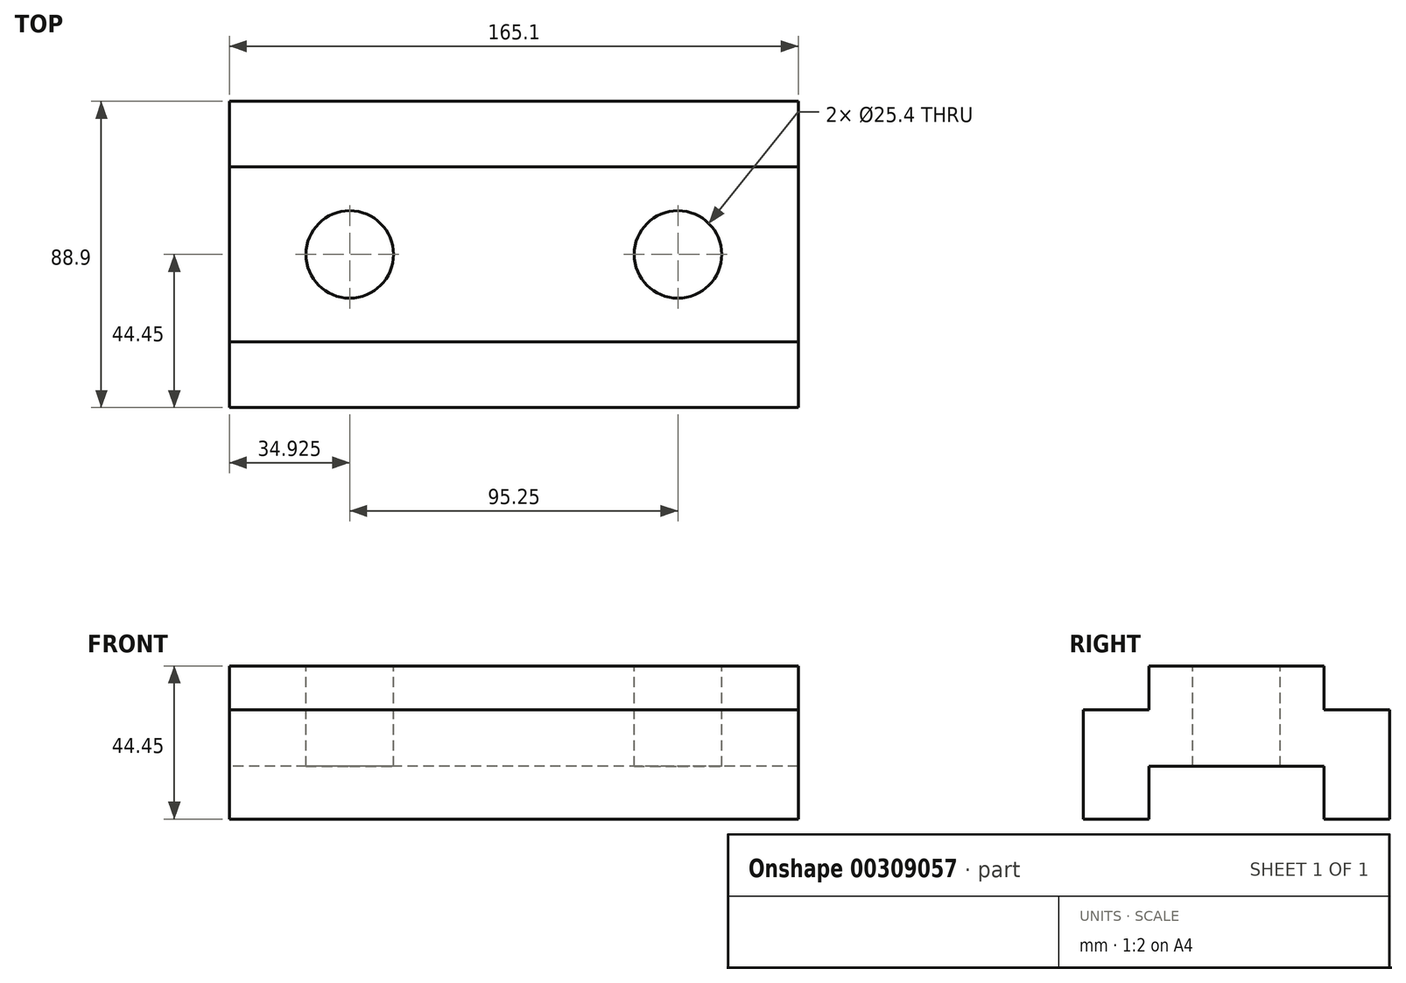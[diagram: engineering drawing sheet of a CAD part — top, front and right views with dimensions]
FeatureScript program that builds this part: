
annotation { "Feature Type Name" : "Feature", "Feature Type Description" : "" }
export const myFeature = defineFeature(function(context is Context, id is Id, definition is map)
    precondition{}
    {
        {
            var Q0;
            Q0=qCreatedBy(makeId("Right.planeOp"),FACE);
            var sketch = newSketch(context, id + "F0", { "sketchPlane" : qUnion([Q0])});
            skLineSegment(sketch, "E0", {"start": v(0, 0) * mm, "end": v(0, 31.75) * mm});
            skLineSegment(sketch, "E1", {"start": v(0, 31.75) * mm, "end": v(19.05, 31.75) * mm});
            skLineSegment(sketch, "E2", {"start": v(19.05, 31.75) * mm, "end": v(19.05, 44.45) * mm});
            skLineSegment(sketch, "E3", {"start": v(19.05, 44.45) * mm, "end": v(69.85, 44.45) * mm});
            skLineSegment(sketch, "E4", {"start": v(69.85, 44.45) * mm, "end": v(69.85, 31.75) * mm});
            skLineSegment(sketch, "E5", {"start": v(69.85, 31.75) * mm, "end": v(88.9, 31.75) * mm});
            skLineSegment(sketch, "E6", {"start": v(88.9, 31.75) * mm, "end": v(88.9, 0) * mm});
            skLineSegment(sketch, "E7", {"start": v(88.9, 0) * mm, "end": v(69.85, 0) * mm});
            skLineSegment(sketch, "E8", {"start": v(69.85, 0) * mm, "end": v(69.85, 15.3) * mm});
            skLineSegment(sketch, "E9", {"start": v(69.85, 15.3) * mm, "end": v(19.05, 15.3) * mm});
            skLineSegment(sketch, "E10", {"start": v(19.05, 15.3) * mm, "end": v(19.05, 0) * mm});
            skLineSegment(sketch, "E11", {"start": v(19.05, 0) * mm, "end": v(0, 0) * mm});
            skSolve(sketch);
        }
        {
            var Q0;
            Q0 = qSketchRegion(id + "F0", true);
            extrude(context, id + "F1", {"entities" : qUnion([Q0]), "depth" : 165.1 * mm});
        }
        {
            var Q0;
            Q0=makeQuery(id+"F1.opExtrude","SWEPT_FACE",FACE,{"disambiguationData":[OSD([sQuery(id+"F0.wireOp",EDGE,"E3")])]});
            var sketch = newSketch(context, id + "F2", { "sketchPlane" : qUnion([Q0])});
            skCircle(sketch, "E12", {"center": v(34.93, 44.45) * mm, "radius": 12.7 * mm});
            skCircle(sketch, "E13", {"center": v(130.18, 44.45) * mm, "radius": 12.7 * mm});
            skSolve(sketch);
        }
        {
            var Q0;
            Q0=makeQuery(id+"F2.imprint","IMPRINT",FACE,{"disambiguationData":[TD([[makeQuery(id+"F2.imprint","IMPRINT",EDGE,{"derivedFrom":sQuery(id+"F2.wireOp",EDGE,"E12")}),1.0]])]});
            var Q1;
            Q1=makeQuery(id+"F2.imprint","IMPRINT",FACE,{"disambiguationData":[TD([[makeQuery(id+"F2.imprint","IMPRINT",EDGE,{"derivedFrom":sQuery(id+"F2.wireOp",EDGE,"E13")}),1.0]])]});
            extrude(context, id + "F3", {"entities" : qUnion([Q0, Q1]), "operationType" : NewBodyOperationType.REMOVE, "endBound" : BoundingType.UP_TO_NEXT, "oppositeDirection" : true, "depth" : 25.4 * mm});
        }
    });
